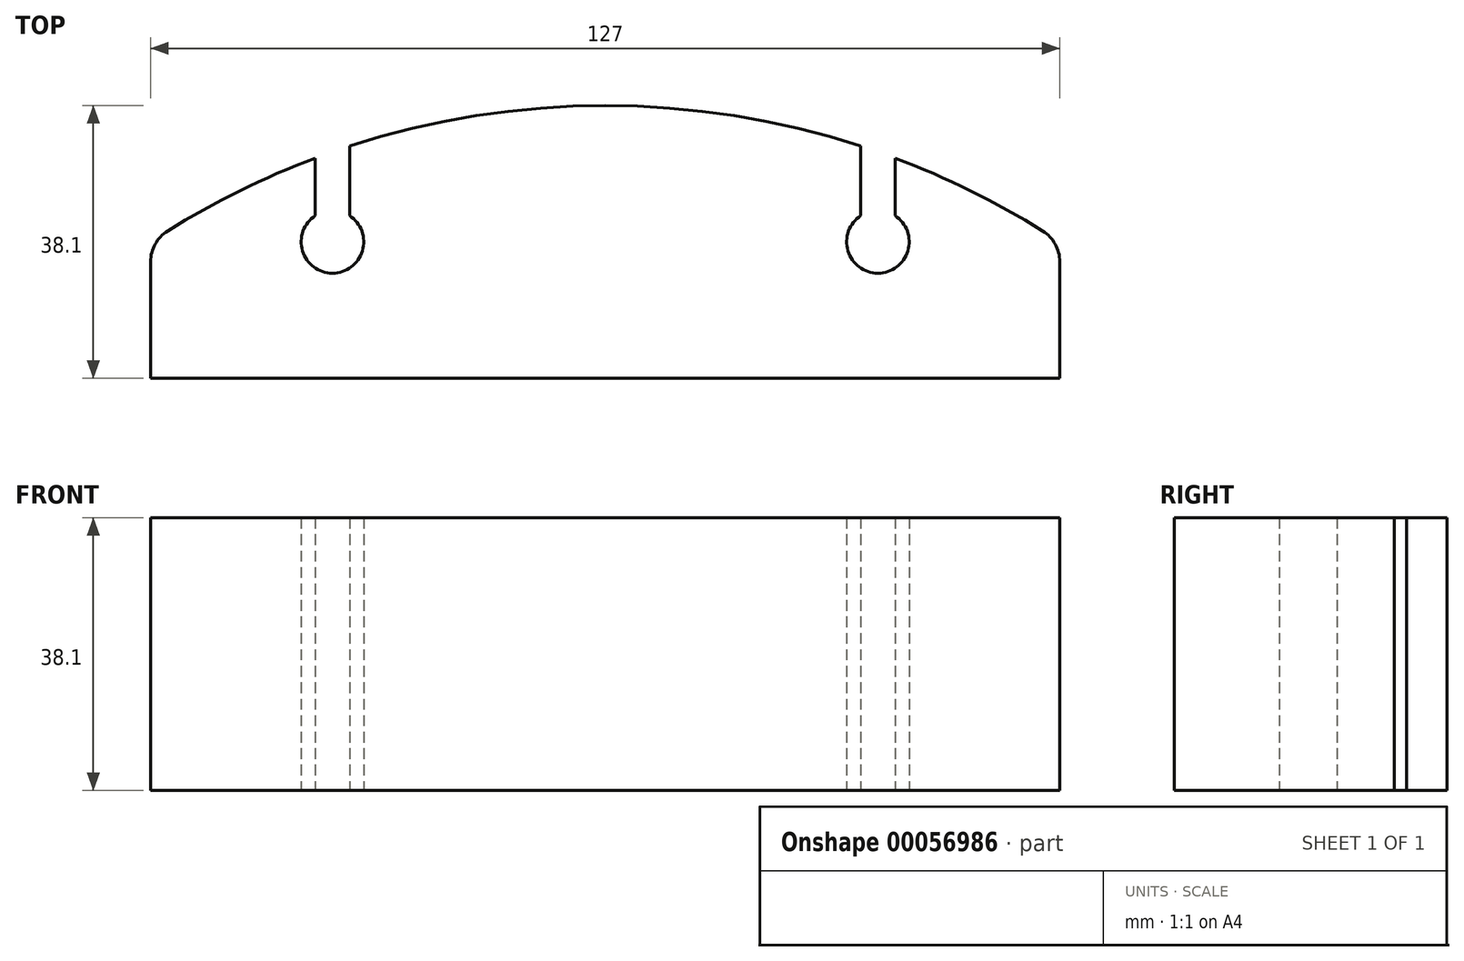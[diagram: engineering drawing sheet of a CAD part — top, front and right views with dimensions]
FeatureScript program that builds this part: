
annotation { "Feature Type Name" : "Feature", "Feature Type Description" : "" }
export const myFeature = defineFeature(function(context is Context, id is Id, definition is map)
    precondition{}
    {
        {
            var Q0;
            Q0=qCreatedBy(makeId("Top.planeOp"),FACE);
            var sketch = newSketch(context, id + "F0", { "sketchPlane" : qUnion([Q0])});
            skLineSegment(sketch, "E0.bottom", {"start": v(-50.72, 0) * mm, "end": v(76.28, 0) * mm});
            skLineSegment(sketch, "E0.left", {"start": v(-50.72, 0) * mm, "end": v(-50.72, 19.05) * mm});
            skLineSegment(sketch, "E0.right", {"start": v(76.28, 0) * mm, "end": v(76.28, 19.05) * mm});
            skArc(sketch, "E1", {"start": v(76.28, 19.05) * mm, "mid": v(65.1, 25.55) * mm, "end": v(53.27, 30.76) * mm});
            skArc(sketch, "E2", {"start": v(48.5, 22.7) * mm, "mid": v(50.88, 14.68) * mm, "end": v(53.27, 22.7) * mm});
            skLineSegment(sketch, "E3", {"start": v(48.5, 32.43) * mm, "end": v(48.5, 22.7) * mm});
            skLineSegment(sketch, "E4", {"start": v(53.27, 30.76) * mm, "end": v(53.27, 22.7) * mm});
            skArc(sketch, "E5.trimOffspring", {"start": v(48.5, 32.43) * mm, "mid": v(12.78, 38.1) * mm, "end": v(-22.93, 32.43) * mm});
            skArc(sketch, "E6", {"start": v(-27.7, 22.7) * mm, "mid": v(-25.32, 14.68) * mm, "end": v(-22.93, 22.7) * mm});
            skLineSegment(sketch, "E7", {"start": v(-27.7, 30.76) * mm, "end": v(-27.7, 22.7) * mm});
            skLineSegment(sketch, "E8", {"start": v(-22.93, 32.43) * mm, "end": v(-22.93, 22.7) * mm});
            skArc(sketch, "E9.trimOffspring", {"start": v(-27.7, 30.76) * mm, "mid": v(-39.54, 25.55) * mm, "end": v(-50.72, 19.05) * mm});
            skSolve(sketch);
        }
        {
            var Q0;
            Q0=makeQuery(id+"F0.imprint","IMPRINT",FACE,{"disambiguationData":[TD([[makeQuery(id+"F0.imprint","IMPRINT",EDGE,{"derivedFrom":sQuery(id+"F0.wireOp",EDGE,"E0.bottom")}),1.0]])]});
            extrude(context, id + "F1", {"entities" : qUnion([Q0]), "depth" : 38.1 * mm});
        }
        {
            var Q0;
            Q0=makeQuery(id+"F1.opExtrude","SWEPT_EDGE",EDGE,{"disambiguationData":[OSD([sQuery(id+"F0.wireOp",EDGE,"E0.left"),sQuery(id+"F0.wireOp",EDGE,"E9.trimOffspring")])]});
            fillet(context, id + "F2", {"entities" : qUnion([Q0]), "radius" : 5.08 * mm, "tangentPropagation" : true, "allowEdgeOverflow" : false});
        }
        {
            var Q0;
            Q0=makeQuery(id+"F1.opExtrude","SWEPT_EDGE",EDGE,{"disambiguationData":[OSD([sQuery(id+"F0.wireOp",EDGE,"E0.right"),sQuery(id+"F0.wireOp",EDGE,"E1")])]});
            fillet(context, id + "F3", {"entities" : qUnion([Q0]), "radius" : 5.08 * mm, "tangentPropagation" : true, "allowEdgeOverflow" : false});
        }
    });
